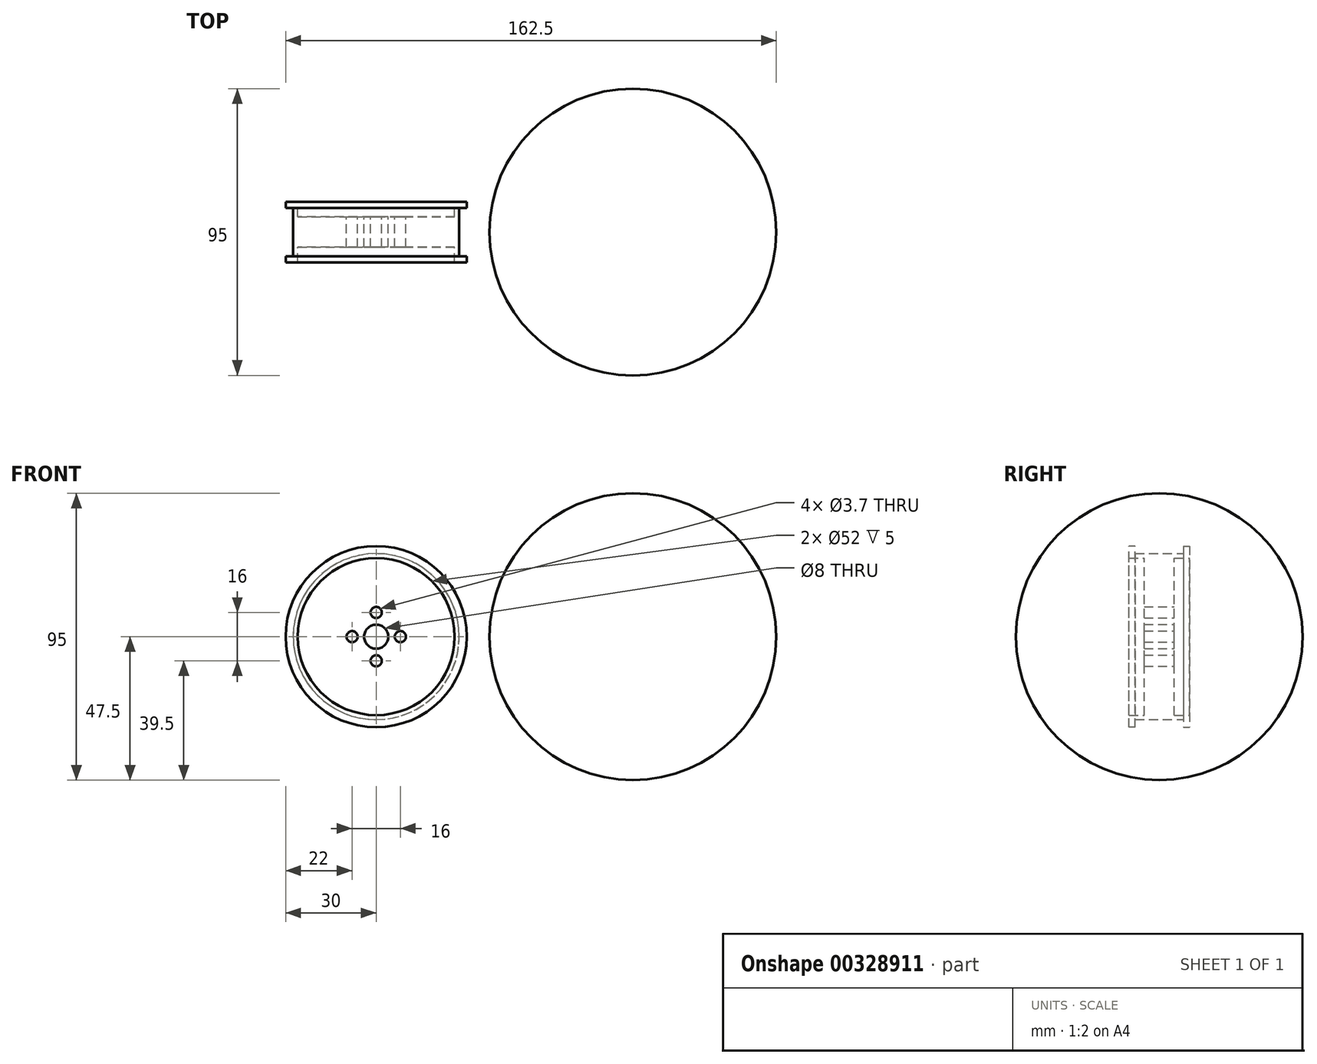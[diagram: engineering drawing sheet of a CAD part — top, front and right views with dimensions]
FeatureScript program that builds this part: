
annotation { "Feature Type Name" : "Feature", "Feature Type Description" : "" }
export const myFeature = defineFeature(function(context is Context, id is Id, definition is map)
    precondition{}
    {
        {
            var Q0;
            Q0=qCreatedBy(makeId("Front.planeOp"),FACE);
            var sketch = newSketch(context, id + "F0", { "sketchPlane" : qUnion([Q0])});
            skLineSegment(sketch, "E0", {"start": v(0, 0) * mm, "end": v(-80, 0) * mm, "construction": true});
            skLineSegment(sketch, "E1", {"start": v(0, 0) * mm, "end": v(80, 0) * mm, "construction": true});
            skSolve(sketch);
        }
        {
            var Q0;
            Q0=qCreatedBy(makeId("Front.planeOp"),FACE);
            var sketch = newSketch(context, id + "F1", { "sketchPlane" : qUnion([Q0])});
            skLineSegment(sketch, "E2.0", {"start": v(0, 0) * mm, "end": v(-80, 0) * mm});
            skLineSegment(sketch, "E3.0", {"start": v(0, 0) * mm, "end": v(80, 0) * mm});
            skLineSegment(sketch, "E4", {"start": v(80, 0) * mm, "end": v(-15, 0) * mm, "construction": true});
            skLineSegment(sketch, "E5", {"start": v(-15, 0) * mm, "end": v(-25, 0) * mm, "construction": true});
            skCircle(sketch, "E6", {"center": v(32.5, 0) * mm, "radius": 47.5 * mm});
            skSolve(sketch);
        }
        {
            var Q0;
            Q0=qCreatedBy(makeId("Front.planeOp"),FACE);
            var sketch = newSketch(context, id + "F2", { "sketchPlane" : qUnion([Q0])});
            skPoint(sketch, "E7.0", {"position": v(-80, 0) * mm});
            skPoint(sketch, "E8.0", {"position": v(-15, 0) * mm});
            skPoint(sketch, "E9.0", {"position": v(-25, 0) * mm});
            skLineSegment(sketch, "E10", {"start": v(-80, 0) * mm, "end": v(-25, 0) * mm, "construction": true});
            skCircle(sketch, "E11", {"center": v(-52.5, 0) * mm, "radius": 27.5 * mm, "construction": true});
            skCircle(sketch, "E12", {"center": v(-52.5, 0) * mm, "radius": 26 * mm});
            skSolve(sketch);
        }
        {
            var Q0;
            Q0=makeQuery(id+"F2.imprint","IMPRINT",FACE,{"disambiguationData":[TD([[makeQuery(id+"F2.imprint","IMPRINT",EDGE,{"derivedFrom":sQuery(id+"F2.wireOp",EDGE,"E12")}),1.0]])]});
            var sketch = newSketch(context, id + "F3", { "sketchPlane" : qUnion([Q0])});
            skCircle(sketch, "E13.0", {"center": v(-52.5, 0) * mm, "radius": 26 * mm});
            skCircle(sketch, "E14", {"center": v(-52.5, 0) * mm, "radius": 4 * mm});
            skLineSegment(sketch, "E15", {"start": v(-52.5, 0) * mm, "end": v(-52.5, 8) * mm, "construction": true});
            skCircle(sketch, "E16", {"center": v(-52.5, 8) * mm, "radius": 1.85 * mm});
            skCircle(sketch, "E17", {"center": v(-52.5, 0) * mm, "radius": 8 * mm, "construction": true});
            skCircle(sketch, "E18.1.0", {"center": v(-44.5, 0) * mm, "radius": 1.85 * mm});
            skCircle(sketch, "E18.2.0", {"center": v(-52.5, -8) * mm, "radius": 1.85 * mm});
            skCircle(sketch, "E18.3.0", {"center": v(-60.5, 0) * mm, "radius": 1.85 * mm});
            skLineSegment(sketch, "E18.anchor2", {"start": v(-52.5, 0) * mm, "end": v(-60.5, 0) * mm, "construction": true});
            skSolve(sketch);
        }
        {
            var Q0;
            Q0=makeQuery(id+"F3.imprint","IMPRINT",FACE,{"disambiguationData":[TD([[makeQuery(id+"F3.imprint","IMPRINT",EDGE,{"derivedFrom":sQuery(id+"F3.wireOp",EDGE,"E13.0")}),1.0]])]});
            extrude(context, id + "F4", {"entities" : qUnion([Q0]), "endBound" : BoundingType.SYMMETRIC, "depth" : 10 * mm});
        }
        {
            var Q0;
            Q0=makeQuery(id+"F4.opExtrude","CAP_FACE",FACE,{"disambiguationData":[OSD([sQuery(id+"F3.wireOp",EDGE,"E13.0"),sQuery(id+"F3.wireOp",EDGE,"E14"),sQuery(id+"F3.wireOp",EDGE,"E16"),sQuery(id+"F3.wireOp",EDGE,"E18.1.0"),sQuery(id+"F3.wireOp",EDGE,"E18.2.0"),sQuery(id+"F3.wireOp",EDGE,"E18.3.0")])],"isStart":false});
            var sketch = newSketch(context, id + "F5", { "sketchPlane" : qUnion([Q0])});
            skCircle(sketch, "E19.0", {"center": v(-52.5, 0) * mm, "radius": 27.5 * mm});
            skCircle(sketch, "E20.0", {"center": v(-52.5, 0) * mm, "radius": 26 * mm});
            skSolve(sketch);
        }
        {
            var Q0;
            Q0=qCreatedBy(makeId("Front.planeOp"),FACE);
            var sketch = newSketch(context, id + "F6", { "sketchPlane" : qUnion([Q0])});
            skCircle(sketch, "E21.0", {"center": v(-52.5, 0) * mm, "radius": 26 * mm});
            skCircle(sketch, "E22.0", {"center": v(-52.5, 0) * mm, "radius": 27.5 * mm});
            skSolve(sketch);
        }
        {
            var Q0;
            Q0=makeQuery(id+"F6.imprint","IMPRINT",FACE,{"disambiguationData":[TD([[makeQuery(id+"F6.imprint","IMPRINT",EDGE,{"derivedFrom":sQuery(id+"F6.wireOp",EDGE,"E21.0")}),-1.0]])]});
            extrude(context, id + "F7", {"entities" : qUnion([Q0]), "operationType" : NewBodyOperationType.ADD, "endBound" : BoundingType.SYMMETRIC, "depth" : 20 * mm});
        }
        {
            var Q0;
            Q0=makeQuery(id+"F7.opExtrude","CAP_FACE",FACE,{"disambiguationData":[OSD([sQuery(id+"F6.wireOp",EDGE,"E21.0"),sQuery(id+"F6.wireOp",EDGE,"E22.0")])],"isStart":false});
            var sketch = newSketch(context, id + "F8", { "sketchPlane" : qUnion([Q0])});
            skCircle(sketch, "E23.0", {"center": v(-52.5, 0) * mm, "radius": 26 * mm});
            skCircle(sketch, "E24", {"center": v(-52.5, 0) * mm, "radius": 30 * mm});
            skCircle(sketch, "E25.0", {"center": v(-52.5, 0) * mm, "radius": 27.5 * mm, "construction": true});
            skSolve(sketch);
        }
        {
            var Q0;
            Q0=makeQuery(id+"F8.imprint","IMPRINT",FACE,{"disambiguationData":[TD([[makeQuery(id+"F8.imprint","IMPRINT",EDGE,{"derivedFrom":sQuery(id+"F8.wireOp",EDGE,"E24")}),1.0]])]});
            extrude(context, id + "F9", {"entities" : qUnion([Q0]), "operationType" : NewBodyOperationType.ADD, "oppositeDirection" : true, "depth" : 2 * mm});
        }
        {
            var Q0;
            Q0=makeQuery(id+"F7.opExtrude","CAP_FACE",FACE,{"disambiguationData":[OSD([sQuery(id+"F6.wireOp",EDGE,"E21.0"),sQuery(id+"F6.wireOp",EDGE,"E22.0")])],"isStart":true});
            var sketch = newSketch(context, id + "F10", { "sketchPlane" : qUnion([Q0])});
            skPoint(sketch, "E26.0", {"position": v(52.5, 0) * mm});
            skCircle(sketch, "E27", {"center": v(52.5, 0) * mm, "radius": 30 * mm});
            skSolve(sketch);
        }
        {
            var Q0;
            Q0=makeQuery(id+"F10.imprint","IMPRINT",FACE,{"disambiguationData":[TD([[makeQuery(id+"F10.imprint","IMPRINT",EDGE,{"derivedFrom":sQuery(id+"F10.wireOp",EDGE,"E27")}),1.0]])]});
            extrude(context, id + "F11", {"entities" : qUnion([Q0]), "operationType" : NewBodyOperationType.ADD, "oppositeDirection" : true, "depth" : 2 * mm});
        }
        {
            var Q0;
            {var subQ0=sQuery(id+"F1.wireOp",EDGE,"E3.0");Q0=makeQuery(id+"F1.imprint","IMPRINT",FACE,{"disambiguationData":[TD([[makeQuery(id+"F1.imprint","IMPRINT",EDGE,{"derivedFrom":subQ0}),1.0]])]});}
            var Q1;
            Q1=sQuery(id+"F1.wireOp",EDGE,"E3.0");
            revolve(context, id + "F12", {"entities" : qUnion([Q0]), "axis" : qUnion([Q1]), "revolveType" : RevolveType.FULL});
        }
    });
